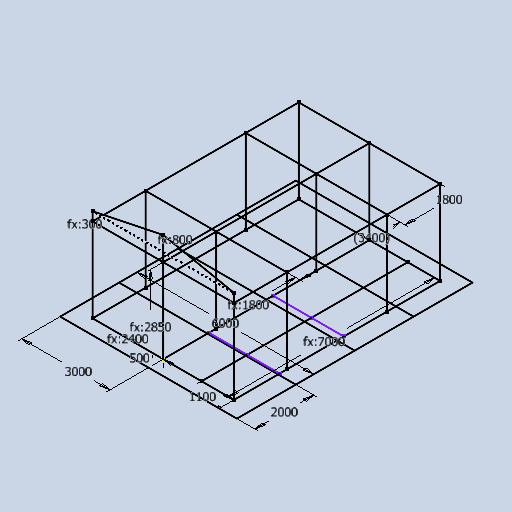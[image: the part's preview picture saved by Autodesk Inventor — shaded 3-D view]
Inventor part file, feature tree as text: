
AUTODESK INVENTOR PART (.ipt)
format: ipt  version: 2025.1 (Build 291241020, 241B)  size: 128,000 bytes
history: native  units: mm
features: sketch x2
ambient origin geometry x8: Origin, YZ Plane, XZ Plane, XY Plane, X Axis, Y Axis, Z Axis, Center Point
feature tree (2):
  sketch  "3D Sketch1"
  sketch  "Sketch2"  dims[d0=2400.0mm d1=7000.0mm d2=2850.0mm d3=300.0mm d5=800.0mm d6=1800.0mm d7=1800.0mm d10=1100.0mm d11=3400.0mm d12=6000.0mm d13=2000.0mm d15=500.0mm d16=3000.0mm]
